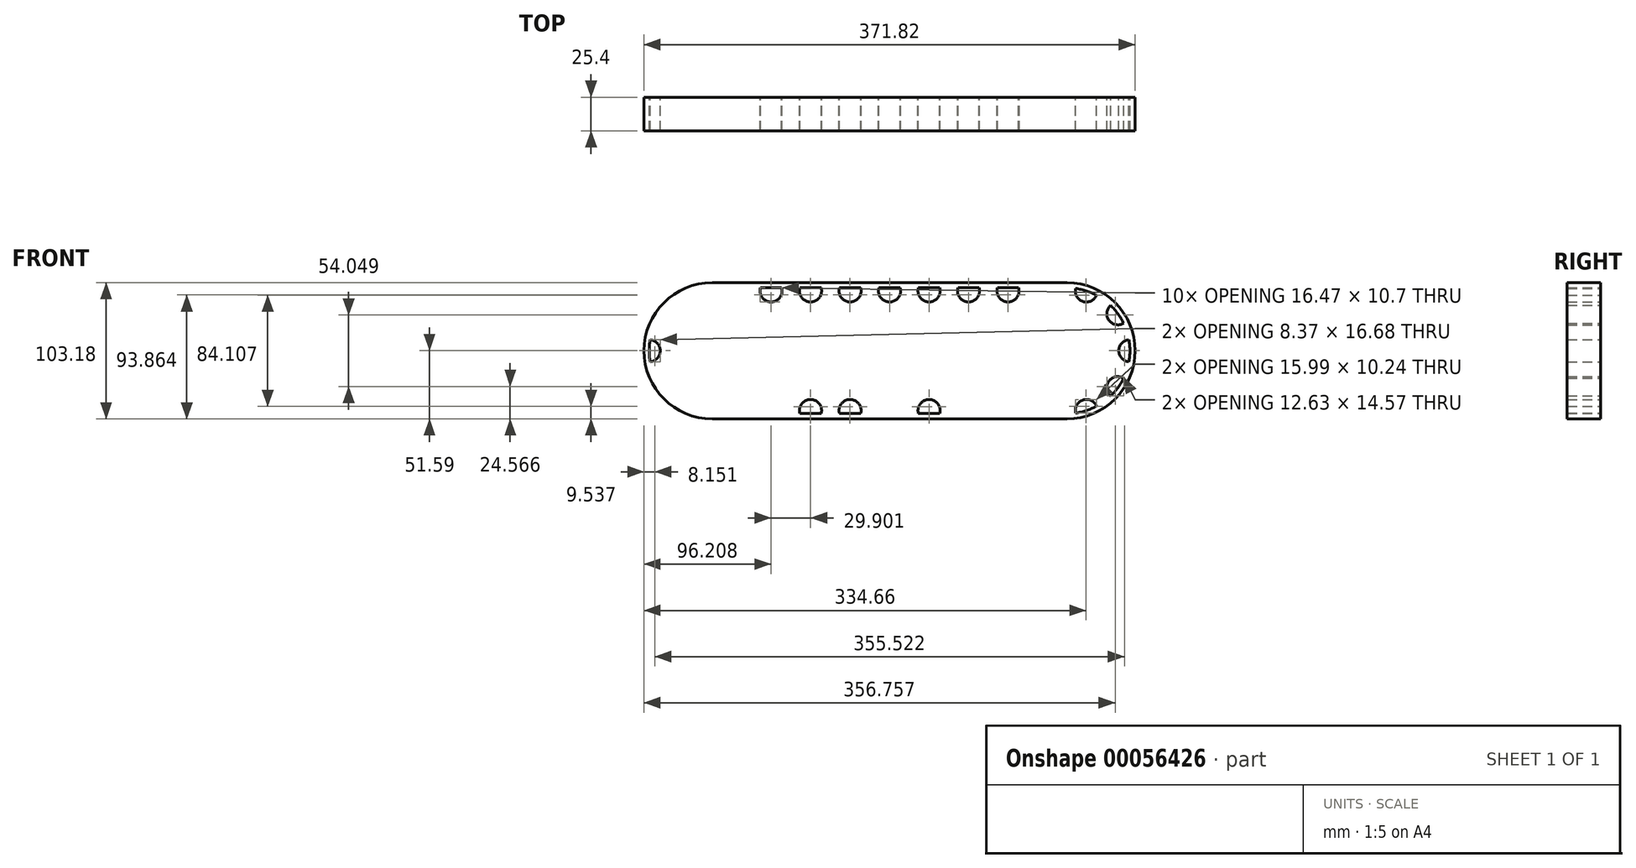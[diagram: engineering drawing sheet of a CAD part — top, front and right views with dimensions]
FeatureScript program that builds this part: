
annotation { "Feature Type Name" : "Feature", "Feature Type Description" : "" }
export const myFeature = defineFeature(function(context is Context, id is Id, definition is map)
    precondition{}
    {
        {
            var Q0;
            Q0=qCreatedBy(makeId("Front.planeOp"),FACE);
            var sketch = newSketch(context, id + "F0", { "sketchPlane" : qUnion([Q0])});
            skCircle(sketch, "E0", {"center": v(0, 0) * mm, "radius": 9.53 * mm});
            skCircle(sketch, "E1", {"center": v(0, 0) * mm, "radius": 15.88 * mm});
            skCircle(sketch, "E2", {"center": v(0, 0) * mm, "radius": 25.4 * mm});
            skCircle(sketch, "E3", {"center": v(0, 0) * mm, "radius": 38.1 * mm});
            skArc(sketch, "E4", {"start": v(5.87, 47.26) * mm, "mid": v(0, 47.63) * mm, "end": v(-5.87, 47.26) * mm});
            skLineSegment(sketch, "E5", {"start": v(-5.87, 47.26) * mm, "end": v(-7.62, 37.33) * mm});
            skLineSegment(sketch, "E6", {"start": v(5.87, 47.26) * mm, "end": v(7.62, 37.33) * mm});
            skLineSegment(sketch, "E7.1.0", {"start": v(-32.53, 34.79) * mm, "end": v(-28.1, 25.72) * mm});
            skArc(sketch, "E7.1.1", {"start": v(-23.03, 41.69) * mm, "mid": v(-28, 38.53) * mm, "end": v(-32.53, 34.79) * mm});
            skLineSegment(sketch, "E7.1.2", {"start": v(-23.03, 41.69) * mm, "end": v(-15.78, 34.68) * mm});
            skLineSegment(sketch, "E7.2.0", {"start": v(-46.76, 9.02) * mm, "end": v(-37.86, 4.29) * mm});
            skArc(sketch, "E7.2.1", {"start": v(-43.14, 20.19) * mm, "mid": v(-45.3, 14.72) * mm, "end": v(-46.76, 9.02) * mm});
            skLineSegment(sketch, "E7.2.2", {"start": v(-43.14, 20.19) * mm, "end": v(-33.15, 18.78) * mm});
            skLineSegment(sketch, "E7.3.0", {"start": v(-43.14, -20.19) * mm, "end": v(-33.15, -18.78) * mm});
            skArc(sketch, "E7.3.1", {"start": v(-46.76, -9.02) * mm, "mid": v(-45.3, -14.72) * mm, "end": v(-43.14, -20.19) * mm});
            skLineSegment(sketch, "E7.3.2", {"start": v(-46.76, -9.02) * mm, "end": v(-37.86, -4.29) * mm});
            skLineSegment(sketch, "E7.4.0", {"start": v(-23.03, -41.69) * mm, "end": v(-15.78, -34.68) * mm});
            skArc(sketch, "E7.4.1", {"start": v(-32.53, -34.79) * mm, "mid": v(-28, -38.53) * mm, "end": v(-23.03, -41.69) * mm});
            skLineSegment(sketch, "E7.4.2", {"start": v(-32.53, -34.79) * mm, "end": v(-28.1, -25.72) * mm});
            skLineSegment(sketch, "E7.5.0", {"start": v(5.87, -47.26) * mm, "end": v(7.62, -37.33) * mm});
            skArc(sketch, "E7.5.1", {"start": v(-5.87, -47.26) * mm, "mid": v(0, -47.63) * mm, "end": v(5.87, -47.26) * mm});
            skLineSegment(sketch, "E7.5.2", {"start": v(-5.87, -47.26) * mm, "end": v(-7.62, -37.33) * mm});
            skLineSegment(sketch, "E7.6.0", {"start": v(32.53, -34.79) * mm, "end": v(28.1, -25.72) * mm});
            skArc(sketch, "E7.6.1", {"start": v(23.03, -41.69) * mm, "mid": v(28, -38.53) * mm, "end": v(32.53, -34.79) * mm});
            skLineSegment(sketch, "E7.6.2", {"start": v(23.03, -41.69) * mm, "end": v(15.78, -34.68) * mm});
            skLineSegment(sketch, "E7.7.0", {"start": v(46.76, -9.02) * mm, "end": v(37.86, -4.29) * mm});
            skArc(sketch, "E7.7.1", {"start": v(43.14, -20.19) * mm, "mid": v(45.3, -14.72) * mm, "end": v(46.76, -9.02) * mm});
            skLineSegment(sketch, "E7.7.2", {"start": v(43.14, -20.19) * mm, "end": v(33.15, -18.78) * mm});
            skLineSegment(sketch, "E7.8.0", {"start": v(43.14, 20.19) * mm, "end": v(33.15, 18.78) * mm});
            skArc(sketch, "E7.8.1", {"start": v(46.76, 9.02) * mm, "mid": v(45.3, 14.72) * mm, "end": v(43.14, 20.19) * mm});
            skLineSegment(sketch, "E7.8.2", {"start": v(46.76, 9.02) * mm, "end": v(37.86, 4.29) * mm});
            skLineSegment(sketch, "E7.9.0", {"start": v(23.03, 41.69) * mm, "end": v(15.78, 34.68) * mm});
            skArc(sketch, "E7.9.1", {"start": v(32.53, 34.79) * mm, "mid": v(28, 38.53) * mm, "end": v(23.03, 41.69) * mm});
            skLineSegment(sketch, "E7.9.2", {"start": v(32.53, 34.79) * mm, "end": v(28.1, 25.72) * mm});
            skLineSegment(sketch, "E8", {"start": v(-3.98, 25.09) * mm, "end": v(-3.98, 15.37) * mm, "construction": true});
            skLineSegment(sketch, "E9", {"start": v(3.98, 25.09) * mm, "end": v(3.98, 15.37) * mm, "construction": true});
            skLineSegment(sketch, "E10.1.0", {"start": v(-19.74, -15.99) * mm, "end": v(-11.32, -11.13) * mm, "construction": true});
            skLineSegment(sketch, "E10.1.1", {"start": v(-23.71, -9.1) * mm, "end": v(-15.3, -4.24) * mm, "construction": true});
            skLineSegment(sketch, "E10.2.0", {"start": v(23.71, -9.1) * mm, "end": v(15.3, -4.24) * mm, "construction": true});
            skLineSegment(sketch, "E10.2.1", {"start": v(19.74, -15.99) * mm, "end": v(11.32, -11.13) * mm, "construction": true});
            skSolve(sketch);
        }
        {
            var Q0;
            Q0=qCreatedBy(makeId("Front.planeOp"),FACE);
            var sketch = newSketch(context, id + "F1", { "sketchPlane" : qUnion([Q0])});
            skArc(sketch, "E11", {"start": v(23.03, 41.69) * mm, "mid": v(-10.34, 46.49) * mm, "end": v(-38.53, 28) * mm});
            skLineSegment(sketch, "E12.0", {"start": v(23.03, 41.69) * mm, "end": v(15.78, 34.68) * mm, "construction": true});
            skLineSegment(sketch, "E12.1", {"start": v(5.87, 47.26) * mm, "end": v(7.62, 37.33) * mm, "construction": true});
            skLineSegment(sketch, "E12.2", {"start": v(-5.87, 47.26) * mm, "end": v(-7.62, 37.33) * mm, "construction": true});
            skLineSegment(sketch, "E12.3", {"start": v(-23.03, 41.69) * mm, "end": v(-15.78, 34.68) * mm, "construction": true});
            skLineSegment(sketch, "E12.4", {"start": v(-32.53, 34.79) * mm, "end": v(-28.1, 25.72) * mm, "construction": true});
            skLineSegment(sketch, "E12.5", {"start": v(-43.14, 20.19) * mm, "end": v(-33.15, 18.78) * mm, "construction": true});
            skLineSegment(sketch, "E12.6", {"start": v(-46.76, 9.02) * mm, "end": v(-37.86, 4.29) * mm, "construction": true});
            skLineSegment(sketch, "E12.7", {"start": v(-46.76, -9.02) * mm, "end": v(-37.86, -4.29) * mm, "construction": true});
            skCircle(sketch, "E13", {"center": v(-14.72, 45.3) * mm, "radius": 8.37 * mm});
            skCircle(sketch, "E14", {"center": v(-38.53, 28) * mm, "radius": 8.37 * mm});
            skCircle(sketch, "E15", {"center": v(-47.62, 0) * mm, "radius": 8.37 * mm});
            skCircle(sketch, "E16", {"center": v(14.72, 45.3) * mm, "radius": 8.37 * mm});
            skLineSegment(sketch, "E17", {"start": v(-14.72, 45.3) * mm, "end": v(14.72, 45.3) * mm, "construction": true});
            skArc(sketch, "E18.trimOffspring", {"start": v(-47.62, 0) * mm, "mid": v(-24.2, -41.02) * mm, "end": v(23.03, -41.69) * mm});
            skArc(sketch, "E19.trimOffspring", {"start": v(-42.84, 20.81) * mm, "mid": v(-45.3, 14.72) * mm, "end": v(-46.89, 8.34) * mm});
            skLineSegment(sketch, "E20", {"start": v(14.72, 45.3) * mm, "end": v(44.62, 45.3) * mm, "construction": true});
            skLineSegment(sketch, "E21", {"start": v(44.62, 45.3) * mm, "end": v(74.52, 45.3) * mm, "construction": true});
            skLineSegment(sketch, "E22", {"start": v(74.52, 45.3) * mm, "end": v(104.42, 45.3) * mm, "construction": true});
            skLineSegment(sketch, "E23", {"start": v(104.42, 45.3) * mm, "end": v(134.32, 45.3) * mm, "construction": true});
            skCircle(sketch, "E24", {"center": v(44.62, 45.3) * mm, "radius": 8.37 * mm});
            skCircle(sketch, "E25", {"center": v(74.52, 45.3) * mm, "radius": 8.37 * mm});
            skCircle(sketch, "E26", {"center": v(104.42, 45.3) * mm, "radius": 8.37 * mm});
            skCircle(sketch, "E27", {"center": v(134.32, 45.3) * mm, "radius": 8.37 * mm});
            skPoint(sketch, "E28", {"position": v(23.09, 45.3) * mm});
            skPoint(sketch, "E29", {"position": v(36.25, 45.3) * mm});
            skLineSegment(sketch, "E30", {"start": v(0, 0) * mm, "end": v(134.32, 0) * mm, "construction": true});
            skLineSegment(sketch, "E31", {"start": v(134.32, 45.3) * mm, "end": v(134.32, 0) * mm, "construction": true});
            skCircle(sketch, "E32.MirrorC", {"center": v(134.32, -45.3) * mm, "radius": 8.37 * mm});
            skCircle(sketch, "E33.MirrorC", {"center": v(104.42, -45.3) * mm, "radius": 8.37 * mm});
            skCircle(sketch, "E34.MirrorC", {"center": v(74.52, -45.3) * mm, "radius": 8.37 * mm});
            skCircle(sketch, "E35.MirrorC", {"center": v(44.62, -45.3) * mm, "radius": 8.37 * mm});
            skCircle(sketch, "E36.MirrorC", {"center": v(14.72, -45.3) * mm, "radius": 8.37 * mm});
            skCircle(sketch, "E37.MirrorC", {"center": v(-14.72, -45.3) * mm, "radius": 8.37 * mm});
            skCircle(sketch, "E38.MirrorC", {"center": v(-38.53, -28) * mm, "radius": 8.37 * mm});
            skCircle(sketch, "E39.MirrorC", {"center": v(164.22, 45.3) * mm, "radius": 8.37 * mm});
            skCircle(sketch, "E40.MirrorC", {"center": v(224.03, 45.3) * mm, "radius": 8.37 * mm});
            skCircle(sketch, "E41.MirrorC", {"center": v(194.12, 45.3) * mm, "radius": 8.37 * mm});
            skCircle(sketch, "E42.MirrorC", {"center": v(253.93, 45.3) * mm, "radius": 8.37 * mm});
            skCircle(sketch, "E43.MirrorC", {"center": v(283.36, 45.3) * mm, "radius": 8.37 * mm});
            skCircle(sketch, "E44.MirrorC", {"center": v(307.17, 28) * mm, "radius": 8.37 * mm});
            skCircle(sketch, "E45.MirrorC", {"center": v(316.27, 0) * mm, "radius": 8.37 * mm});
            skCircle(sketch, "E46.MirrorC", {"center": v(307.17, -28) * mm, "radius": 8.37 * mm});
            skCircle(sketch, "E47.MirrorC", {"center": v(283.36, -45.3) * mm, "radius": 8.37 * mm});
            skCircle(sketch, "E48.MirrorC", {"center": v(253.93, -45.3) * mm, "radius": 8.37 * mm});
            skCircle(sketch, "E49.MirrorC", {"center": v(224.03, -45.3) * mm, "radius": 8.37 * mm});
            skCircle(sketch, "E50.MirrorC", {"center": v(194.12, -45.3) * mm, "radius": 8.37 * mm});
            skCircle(sketch, "E51.MirrorC", {"center": v(164.22, -45.3) * mm, "radius": 8.37 * mm});
            skSolve(sketch);
        }
        {
            var Q0;
            Q0=qCreatedBy(makeId("Front.planeOp"),FACE);
            var sketch = newSketch(context, id + "F2", { "sketchPlane" : qUnion([Q0])});
            skArc(sketch, "E52", {"start": v(0, 47.62) * mm, "mid": v(-47.62, 0) * mm, "end": v(0, -47.62) * mm});
            skLineSegment(sketch, "E53", {"start": v(0, 47.62) * mm, "end": v(268.64, 47.62) * mm});
            skLineSegment(sketch, "E54", {"start": v(0, -47.62) * mm, "end": v(268.64, -47.62) * mm});
            skLineSegment(sketch, "E55.0", {"start": v(134.32, 45.3) * mm, "end": v(134.32, 0) * mm, "construction": true});
            skLineSegment(sketch, "E56.0", {"start": v(0, 0) * mm, "end": v(134.32, 0) * mm, "construction": true});
            skLineSegment(sketch, "E57.MirrorCS", {"start": v(268.64, 0) * mm, "end": v(134.32, 0) * mm, "construction": true});
            skArc(sketch, "E58", {"start": v(268.64, 47.62) * mm, "mid": v(316.27, 0) * mm, "end": v(268.64, -47.62) * mm});
            skArc(sketch, "E59.0", {"start": v(0, 51.59) * mm, "mid": v(-51.59, 0) * mm, "end": v(0, -51.59) * mm});
            skLineSegment(sketch, "E59.1", {"start": v(0, 51.59) * mm, "end": v(268.64, 51.59) * mm});
            skArc(sketch, "E59.2", {"start": v(268.64, 51.59) * mm, "mid": v(320.23, 0) * mm, "end": v(268.64, -51.59) * mm});
            skLineSegment(sketch, "E59.3", {"start": v(0, -51.59) * mm, "end": v(268.64, -51.59) * mm});
            skArc(sketch, "E60.0", {"start": v(-23.04, 46.15) * mm, "mid": v(-12.13, 37.33) * mm, "end": v(-8.49, 50.88) * mm});
            skArc(sketch, "E60.1", {"start": v(-45.77, 23.8) * mm, "mid": v(-31.76, 23.07) * mm, "end": v(-36.77, 36.18) * mm});
            skArc(sketch, "E60.2", {"start": v(9.2, 51.59) * mm, "mid": v(14.72, 36.92) * mm, "end": v(20.24, 51.59) * mm});
            skArc(sketch, "E60.3", {"start": v(39.1, 51.59) * mm, "mid": v(44.62, 36.92) * mm, "end": v(50.14, 51.59) * mm});
            skArc(sketch, "E60.4", {"start": v(69, 51.59) * mm, "mid": v(74.52, 36.92) * mm, "end": v(80.04, 51.59) * mm});
            skArc(sketch, "E60.5", {"start": v(98.9, 51.59) * mm, "mid": v(104.42, 36.92) * mm, "end": v(109.94, 51.59) * mm});
            skArc(sketch, "E60.6", {"start": v(128.8, 51.59) * mm, "mid": v(134.32, 36.92) * mm, "end": v(139.84, 51.59) * mm});
            skArc(sketch, "E60.7", {"start": v(169.74, 51.59) * mm, "mid": v(164.22, 36.92) * mm, "end": v(158.7, 51.59) * mm});
            skArc(sketch, "E60.8", {"start": v(199.65, 51.59) * mm, "mid": v(194.12, 36.92) * mm, "end": v(188.6, 51.59) * mm});
            skArc(sketch, "E60.9", {"start": v(229.55, 51.59) * mm, "mid": v(224.03, 36.92) * mm, "end": v(218.5, 51.59) * mm});
            skArc(sketch, "E60.10", {"start": v(259.45, 51.59) * mm, "mid": v(253.93, 36.92) * mm, "end": v(248.4, 51.59) * mm});
            skArc(sketch, "E60.11", {"start": v(291.69, 46.15) * mm, "mid": v(280.77, 37.33) * mm, "end": v(277.13, 50.88) * mm});
            skArc(sketch, "E60.12", {"start": v(314.42, 23.8) * mm, "mid": v(300.4, 23.07) * mm, "end": v(305.42, 36.18) * mm});
            skArc(sketch, "E60.13", {"start": v(291.69, -46.15) * mm, "mid": v(280.77, -37.33) * mm, "end": v(277.13, -50.88) * mm});
            skArc(sketch, "E60.14", {"start": v(314.42, -23.8) * mm, "mid": v(300.4, -23.07) * mm, "end": v(305.42, -36.18) * mm});
            skArc(sketch, "E60.15", {"start": v(319.66, -7.65) * mm, "mid": v(307.9, 0) * mm, "end": v(319.66, 7.65) * mm});
            skArc(sketch, "E60.16", {"start": v(259.45, -51.59) * mm, "mid": v(253.93, -36.92) * mm, "end": v(248.4, -51.59) * mm});
            skArc(sketch, "E60.17", {"start": v(229.55, -51.59) * mm, "mid": v(224.03, -36.92) * mm, "end": v(218.5, -51.59) * mm});
            skArc(sketch, "E60.18", {"start": v(199.65, -51.59) * mm, "mid": v(194.12, -36.92) * mm, "end": v(188.6, -51.59) * mm});
            skArc(sketch, "E60.19", {"start": v(169.74, -51.59) * mm, "mid": v(164.22, -36.92) * mm, "end": v(158.7, -51.59) * mm});
            skArc(sketch, "E60.20", {"start": v(128.8, -51.59) * mm, "mid": v(134.32, -36.92) * mm, "end": v(139.84, -51.59) * mm});
            skArc(sketch, "E60.21", {"start": v(98.9, -51.59) * mm, "mid": v(104.42, -36.92) * mm, "end": v(109.94, -51.59) * mm});
            skArc(sketch, "E60.22", {"start": v(69, -51.59) * mm, "mid": v(74.52, -36.92) * mm, "end": v(80.04, -51.59) * mm});
            skArc(sketch, "E60.23", {"start": v(39.1, -51.59) * mm, "mid": v(44.62, -36.92) * mm, "end": v(50.14, -51.59) * mm});
            skArc(sketch, "E60.24", {"start": v(9.2, -51.59) * mm, "mid": v(14.72, -36.92) * mm, "end": v(20.24, -51.59) * mm});
            skArc(sketch, "E60.25", {"start": v(-23.04, -46.15) * mm, "mid": v(-12.13, -37.33) * mm, "end": v(-8.49, -50.88) * mm});
            skArc(sketch, "E60.26", {"start": v(-45.77, -23.8) * mm, "mid": v(-31.76, -23.07) * mm, "end": v(-36.77, -36.18) * mm});
            skArc(sketch, "E60.27", {"start": v(-51.02, -7.65) * mm, "mid": v(-39.25, 0) * mm, "end": v(-51.02, 7.65) * mm});
            skSolve(sketch);
        }
        {
            var Q0;
            Q0 = qSketchRegion(id + "F2", true);
            var Q1;
            {var subQ0=sQuery(id+"F2.wireOp",EDGE,"E60.26");var subQ1=sQuery(id+"F2.wireOp",EDGE,"E52");var subQ2=makeQuery(id+"F2.imprint","INTERSECT",VERTEX,{"disambiguationData":[OD(0.0)],"derivedFrom":[subQ1,subQ0]});Q1=makeQuery(id+"F2.imprint","IMPRINT",FACE,{"disambiguationData":[TD([[makeQuery(id+"F2.imprint","IMPRINT",EDGE,{"disambiguationData":[TD([[subQ2,-1.0]])],"derivedFrom":subQ1}),1.0]])]});}
            var Q2;
            {var subQ0=sQuery(id+"F2.wireOp",EDGE,"E60.27");var subQ1=sQuery(id+"F2.wireOp",EDGE,"E52");var subQ2=makeQuery(id+"F2.imprint","INTERSECT",VERTEX,{"disambiguationData":[OD(0.0)],"derivedFrom":[subQ1,subQ0]});Q2=makeQuery(id+"F2.imprint","IMPRINT",FACE,{"disambiguationData":[TD([[makeQuery(id+"F2.imprint","IMPRINT",EDGE,{"disambiguationData":[TD([[subQ2,-1.0]])],"derivedFrom":subQ1}),1.0]])]});}
            var Q3;
            {var subQ0=sQuery(id+"F2.wireOp",EDGE,"E60.25");var subQ1=sQuery(id+"F2.wireOp",EDGE,"E52");var subQ2=makeQuery(id+"F2.imprint","INTERSECT",VERTEX,{"disambiguationData":[OD(0.0)],"derivedFrom":[subQ1,subQ0]});Q3=makeQuery(id+"F2.imprint","IMPRINT",FACE,{"disambiguationData":[TD([[makeQuery(id+"F2.imprint","IMPRINT",EDGE,{"disambiguationData":[TD([[subQ2,-1.0]])],"derivedFrom":subQ1}),1.0]])]});}
            var Q4;
            {var subQ0=sQuery(id+"F2.wireOp",EDGE,"E60.24");var subQ1=sQuery(id+"F2.wireOp",EDGE,"E54");var subQ2=makeQuery(id+"F2.imprint","INTERSECT",VERTEX,{"disambiguationData":[OD(0.0)],"derivedFrom":[subQ1,subQ0]});Q4=makeQuery(id+"F2.imprint","IMPRINT",FACE,{"disambiguationData":[TD([[makeQuery(id+"F2.imprint","IMPRINT",EDGE,{"disambiguationData":[TD([[subQ2,-1.0]])],"derivedFrom":subQ1}),1.0]])]});}
            var Q5;
            {var subQ0=sQuery(id+"F2.wireOp",EDGE,"E60.23");var subQ1=sQuery(id+"F2.wireOp",EDGE,"E54");var subQ2=makeQuery(id+"F2.imprint","INTERSECT",VERTEX,{"disambiguationData":[OD(0.0)],"derivedFrom":[subQ1,subQ0]});Q5=makeQuery(id+"F2.imprint","IMPRINT",FACE,{"disambiguationData":[TD([[makeQuery(id+"F2.imprint","IMPRINT",EDGE,{"disambiguationData":[TD([[subQ2,-1.0]])],"derivedFrom":subQ1}),1.0]])]});}
            var Q6;
            {var subQ0=sQuery(id+"F2.wireOp",EDGE,"E60.22");var subQ1=sQuery(id+"F2.wireOp",EDGE,"E54");var subQ2=makeQuery(id+"F2.imprint","INTERSECT",VERTEX,{"disambiguationData":[OD(0.0)],"derivedFrom":[subQ1,subQ0]});Q6=makeQuery(id+"F2.imprint","IMPRINT",FACE,{"disambiguationData":[TD([[makeQuery(id+"F2.imprint","IMPRINT",EDGE,{"disambiguationData":[TD([[subQ2,-1.0]])],"derivedFrom":subQ1}),1.0]])]});}
            var Q7;
            {var subQ0=sQuery(id+"F2.wireOp",EDGE,"E60.1");var subQ1=sQuery(id+"F2.wireOp",EDGE,"E52");var subQ2=makeQuery(id+"F2.imprint","INTERSECT",VERTEX,{"disambiguationData":[OD(0.0)],"derivedFrom":[subQ1,subQ0]});Q7=makeQuery(id+"F2.imprint","IMPRINT",FACE,{"disambiguationData":[TD([[makeQuery(id+"F2.imprint","IMPRINT",EDGE,{"disambiguationData":[TD([[subQ2,-1.0]])],"derivedFrom":subQ1}),1.0]])]});}
            var Q8;
            {var subQ0=sQuery(id+"F2.wireOp",EDGE,"E60.0");var subQ1=sQuery(id+"F2.wireOp",EDGE,"E52");var subQ2=makeQuery(id+"F2.imprint","INTERSECT",VERTEX,{"disambiguationData":[OD(0.0)],"derivedFrom":[subQ1,subQ0]});Q8=makeQuery(id+"F2.imprint","IMPRINT",FACE,{"disambiguationData":[TD([[makeQuery(id+"F2.imprint","IMPRINT",EDGE,{"disambiguationData":[TD([[subQ2,-1.0]])],"derivedFrom":subQ1}),1.0]])]});}
            var Q9;
            {var subQ0=sQuery(id+"F2.wireOp",EDGE,"E60.2");var subQ1=sQuery(id+"F2.wireOp",EDGE,"E53");var subQ2=makeQuery(id+"F2.imprint","INTERSECT",VERTEX,{"disambiguationData":[OD(0.0)],"derivedFrom":[subQ1,subQ0]});Q9=makeQuery(id+"F2.imprint","IMPRINT",FACE,{"disambiguationData":[TD([[makeQuery(id+"F2.imprint","IMPRINT",EDGE,{"disambiguationData":[TD([[subQ2,-1.0]])],"derivedFrom":subQ1}),-1.0]])]});}
            var Q10;
            {var subQ0=sQuery(id+"F2.wireOp",EDGE,"E60.3");var subQ1=sQuery(id+"F2.wireOp",EDGE,"E53");var subQ2=makeQuery(id+"F2.imprint","INTERSECT",VERTEX,{"disambiguationData":[OD(0.0)],"derivedFrom":[subQ1,subQ0]});Q10=makeQuery(id+"F2.imprint","IMPRINT",FACE,{"disambiguationData":[TD([[makeQuery(id+"F2.imprint","IMPRINT",EDGE,{"disambiguationData":[TD([[subQ2,-1.0]])],"derivedFrom":subQ1}),-1.0]])]});}
            var Q11;
            {var subQ0=sQuery(id+"F2.wireOp",EDGE,"E60.4");var subQ1=sQuery(id+"F2.wireOp",EDGE,"E53");var subQ2=makeQuery(id+"F2.imprint","INTERSECT",VERTEX,{"disambiguationData":[OD(0.0)],"derivedFrom":[subQ1,subQ0]});Q11=makeQuery(id+"F2.imprint","IMPRINT",FACE,{"disambiguationData":[TD([[makeQuery(id+"F2.imprint","IMPRINT",EDGE,{"disambiguationData":[TD([[subQ2,-1.0]])],"derivedFrom":subQ1}),-1.0]])]});}
            var Q12;
            {var subQ0=sQuery(id+"F2.wireOp",EDGE,"E60.5");var subQ1=sQuery(id+"F2.wireOp",EDGE,"E53");var subQ2=makeQuery(id+"F2.imprint","INTERSECT",VERTEX,{"disambiguationData":[OD(0.0)],"derivedFrom":[subQ1,subQ0]});Q12=makeQuery(id+"F2.imprint","IMPRINT",FACE,{"disambiguationData":[TD([[makeQuery(id+"F2.imprint","IMPRINT",EDGE,{"disambiguationData":[TD([[subQ2,-1.0]])],"derivedFrom":subQ1}),-1.0]])]});}
            var Q13;
            {var subQ0=sQuery(id+"F2.wireOp",EDGE,"E60.6");var subQ1=sQuery(id+"F2.wireOp",EDGE,"E53");var subQ2=makeQuery(id+"F2.imprint","INTERSECT",VERTEX,{"disambiguationData":[OD(0.0)],"derivedFrom":[subQ1,subQ0]});Q13=makeQuery(id+"F2.imprint","IMPRINT",FACE,{"disambiguationData":[TD([[makeQuery(id+"F2.imprint","IMPRINT",EDGE,{"disambiguationData":[TD([[subQ2,-1.0]])],"derivedFrom":subQ1}),-1.0]])]});}
            var Q14;
            {var subQ0=sQuery(id+"F2.wireOp",EDGE,"E60.7");var subQ1=sQuery(id+"F2.wireOp",EDGE,"E53");var subQ2=makeQuery(id+"F2.imprint","INTERSECT",VERTEX,{"disambiguationData":[OD(0.0)],"derivedFrom":[subQ1,subQ0]});Q14=makeQuery(id+"F2.imprint","IMPRINT",FACE,{"disambiguationData":[TD([[makeQuery(id+"F2.imprint","IMPRINT",EDGE,{"disambiguationData":[TD([[subQ2,-1.0]])],"derivedFrom":subQ1}),-1.0]])]});}
            var Q15;
            {var subQ0=sQuery(id+"F2.wireOp",EDGE,"E60.8");var subQ1=sQuery(id+"F2.wireOp",EDGE,"E53");var subQ2=makeQuery(id+"F2.imprint","INTERSECT",VERTEX,{"disambiguationData":[OD(0.0)],"derivedFrom":[subQ1,subQ0]});Q15=makeQuery(id+"F2.imprint","IMPRINT",FACE,{"disambiguationData":[TD([[makeQuery(id+"F2.imprint","IMPRINT",EDGE,{"disambiguationData":[TD([[subQ2,-1.0]])],"derivedFrom":subQ1}),-1.0]])]});}
            var Q16;
            {var subQ0=sQuery(id+"F2.wireOp",EDGE,"E60.9");var subQ1=sQuery(id+"F2.wireOp",EDGE,"E53");var subQ2=makeQuery(id+"F2.imprint","INTERSECT",VERTEX,{"disambiguationData":[OD(0.0)],"derivedFrom":[subQ1,subQ0]});Q16=makeQuery(id+"F2.imprint","IMPRINT",FACE,{"disambiguationData":[TD([[makeQuery(id+"F2.imprint","IMPRINT",EDGE,{"disambiguationData":[TD([[subQ2,-1.0]])],"derivedFrom":subQ1}),-1.0]])]});}
            var Q17;
            {var subQ0=sQuery(id+"F2.wireOp",EDGE,"E60.10");var subQ1=sQuery(id+"F2.wireOp",EDGE,"E53");var subQ2=makeQuery(id+"F2.imprint","INTERSECT",VERTEX,{"disambiguationData":[OD(0.0)],"derivedFrom":[subQ1,subQ0]});Q17=makeQuery(id+"F2.imprint","IMPRINT",FACE,{"disambiguationData":[TD([[makeQuery(id+"F2.imprint","IMPRINT",EDGE,{"disambiguationData":[TD([[subQ2,-1.0]])],"derivedFrom":subQ1}),-1.0]])]});}
            var Q18;
            {var subQ0=sQuery(id+"F2.wireOp",EDGE,"E60.11");var subQ1=sQuery(id+"F2.wireOp",EDGE,"E58");var subQ2=makeQuery(id+"F2.imprint","INTERSECT",VERTEX,{"disambiguationData":[OD(0.0)],"derivedFrom":[subQ1,subQ0]});Q18=makeQuery(id+"F2.imprint","IMPRINT",FACE,{"disambiguationData":[TD([[makeQuery(id+"F2.imprint","IMPRINT",EDGE,{"disambiguationData":[TD([[subQ2,-1.0]])],"derivedFrom":subQ1}),-1.0]])]});}
            var Q19;
            {var subQ0=sQuery(id+"F2.wireOp",EDGE,"E60.12");var subQ1=sQuery(id+"F2.wireOp",EDGE,"E58");var subQ2=makeQuery(id+"F2.imprint","INTERSECT",VERTEX,{"disambiguationData":[OD(0.0)],"derivedFrom":[subQ1,subQ0]});Q19=makeQuery(id+"F2.imprint","IMPRINT",FACE,{"disambiguationData":[TD([[makeQuery(id+"F2.imprint","IMPRINT",EDGE,{"disambiguationData":[TD([[subQ2,-1.0]])],"derivedFrom":subQ1}),-1.0]])]});}
            var Q20;
            {var subQ0=sQuery(id+"F2.wireOp",EDGE,"E60.15");var subQ1=sQuery(id+"F2.wireOp",EDGE,"E58");var subQ2=makeQuery(id+"F2.imprint","INTERSECT",VERTEX,{"disambiguationData":[OD(0.0)],"derivedFrom":[subQ1,subQ0]});Q20=makeQuery(id+"F2.imprint","IMPRINT",FACE,{"disambiguationData":[TD([[makeQuery(id+"F2.imprint","IMPRINT",EDGE,{"disambiguationData":[TD([[subQ2,-1.0]])],"derivedFrom":subQ1}),-1.0]])]});}
            var Q21;
            {var subQ0=sQuery(id+"F2.wireOp",EDGE,"E60.14");var subQ1=sQuery(id+"F2.wireOp",EDGE,"E58");var subQ2=makeQuery(id+"F2.imprint","INTERSECT",VERTEX,{"disambiguationData":[OD(0.0)],"derivedFrom":[subQ1,subQ0]});Q21=makeQuery(id+"F2.imprint","IMPRINT",FACE,{"disambiguationData":[TD([[makeQuery(id+"F2.imprint","IMPRINT",EDGE,{"disambiguationData":[TD([[subQ2,-1.0]])],"derivedFrom":subQ1}),-1.0]])]});}
            var Q22;
            {var subQ0=sQuery(id+"F2.wireOp",EDGE,"E60.13");var subQ1=sQuery(id+"F2.wireOp",EDGE,"E58");var subQ2=makeQuery(id+"F2.imprint","INTERSECT",VERTEX,{"disambiguationData":[OD(0.0)],"derivedFrom":[subQ1,subQ0]});Q22=makeQuery(id+"F2.imprint","IMPRINT",FACE,{"disambiguationData":[TD([[makeQuery(id+"F2.imprint","IMPRINT",EDGE,{"disambiguationData":[TD([[subQ2,-1.0]])],"derivedFrom":subQ1}),-1.0]])]});}
            var Q23;
            {var subQ0=sQuery(id+"F2.wireOp",EDGE,"E60.16");var subQ1=sQuery(id+"F2.wireOp",EDGE,"E54");var subQ2=makeQuery(id+"F2.imprint","INTERSECT",VERTEX,{"disambiguationData":[OD(0.0)],"derivedFrom":[subQ1,subQ0]});Q23=makeQuery(id+"F2.imprint","IMPRINT",FACE,{"disambiguationData":[TD([[makeQuery(id+"F2.imprint","IMPRINT",EDGE,{"disambiguationData":[TD([[subQ2,-1.0]])],"derivedFrom":subQ1}),1.0]])]});}
            var Q24;
            {var subQ0=sQuery(id+"F2.wireOp",EDGE,"E60.17");var subQ1=sQuery(id+"F2.wireOp",EDGE,"E54");var subQ2=makeQuery(id+"F2.imprint","INTERSECT",VERTEX,{"disambiguationData":[OD(0.0)],"derivedFrom":[subQ1,subQ0]});Q24=makeQuery(id+"F2.imprint","IMPRINT",FACE,{"disambiguationData":[TD([[makeQuery(id+"F2.imprint","IMPRINT",EDGE,{"disambiguationData":[TD([[subQ2,-1.0]])],"derivedFrom":subQ1}),1.0]])]});}
            var Q25;
            {var subQ0=sQuery(id+"F2.wireOp",EDGE,"E60.18");var subQ1=sQuery(id+"F2.wireOp",EDGE,"E54");var subQ2=makeQuery(id+"F2.imprint","INTERSECT",VERTEX,{"disambiguationData":[OD(0.0)],"derivedFrom":[subQ1,subQ0]});Q25=makeQuery(id+"F2.imprint","IMPRINT",FACE,{"disambiguationData":[TD([[makeQuery(id+"F2.imprint","IMPRINT",EDGE,{"disambiguationData":[TD([[subQ2,-1.0]])],"derivedFrom":subQ1}),1.0]])]});}
            var Q26;
            {var subQ0=sQuery(id+"F2.wireOp",EDGE,"E60.19");var subQ1=sQuery(id+"F2.wireOp",EDGE,"E54");var subQ2=makeQuery(id+"F2.imprint","INTERSECT",VERTEX,{"disambiguationData":[OD(0.0)],"derivedFrom":[subQ1,subQ0]});Q26=makeQuery(id+"F2.imprint","IMPRINT",FACE,{"disambiguationData":[TD([[makeQuery(id+"F2.imprint","IMPRINT",EDGE,{"disambiguationData":[TD([[subQ2,-1.0]])],"derivedFrom":subQ1}),1.0]])]});}
            var Q27;
            {var subQ0=sQuery(id+"F2.wireOp",EDGE,"E60.20");var subQ1=sQuery(id+"F2.wireOp",EDGE,"E54");var subQ2=makeQuery(id+"F2.imprint","INTERSECT",VERTEX,{"disambiguationData":[OD(0.0)],"derivedFrom":[subQ1,subQ0]});Q27=makeQuery(id+"F2.imprint","IMPRINT",FACE,{"disambiguationData":[TD([[makeQuery(id+"F2.imprint","IMPRINT",EDGE,{"disambiguationData":[TD([[subQ2,-1.0]])],"derivedFrom":subQ1}),1.0]])]});}
            var Q28;
            {var subQ0=sQuery(id+"F2.wireOp",EDGE,"E60.21");var subQ1=sQuery(id+"F2.wireOp",EDGE,"E54");var subQ2=makeQuery(id+"F2.imprint","INTERSECT",VERTEX,{"disambiguationData":[OD(0.0)],"derivedFrom":[subQ1,subQ0]});Q28=makeQuery(id+"F2.imprint","IMPRINT",FACE,{"disambiguationData":[TD([[makeQuery(id+"F2.imprint","IMPRINT",EDGE,{"disambiguationData":[TD([[subQ2,-1.0]])],"derivedFrom":subQ1}),1.0]])]});}
            extrude(context, id + "F3", {"entities" : qUnion([Q0, Q1, Q2, Q3, Q4, Q5, Q6, Q7, Q8, Q9, Q10, Q11, Q12, Q13, Q14, Q15, Q16, Q17, Q18, Q19, Q20, Q21, Q22, Q23, Q24, Q25, Q26, Q27, Q28]), "depth" : 25.4 * mm});
        }
    });
